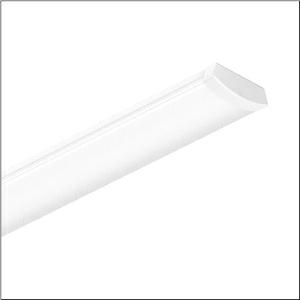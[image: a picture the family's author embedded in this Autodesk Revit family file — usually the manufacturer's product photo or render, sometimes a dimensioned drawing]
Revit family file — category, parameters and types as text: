
# Revit family: siluette_21_51ln12mkm40a
name_source: partatom
category: Lighting Fixtures
units: mm (PartAtom-declared; Revit-internal decimal feet)

## family parameters
Cut with Voids When Loaded = No
Host = Face
Light Source = No
Part Type = Normal
Room Calculation Point = No
Round Connector Dimension = Use Diameter
Shared = No

## types (1)
- --- (1 x LED, 2980 lm, 20.6 W, 5000K)
    Apparent Load = 21 VA
    CIE Flux Codes = 43 73 92 94 100
    Color Rendering = 80
    Color Temperature = 5000K
    Default Elevation = 1800 mm
    Description = Siluette 21, office luminaire, primary optical cover: enclosure, of PC, frosted, light emission: direct distribution, primary light characteristic: symmetric, installation type: suspended mounting, surface-mounted, LED, rated luminous flux: 5.010lm, luminous efficacy: 144lm/W, light colour: 830/840/850, colour temperature: 3000/4000/5000K, control gear: ON/OFF Multilumen, with terminal, 3-pole, mains connection: 220..240V, AC, 50/60Hz, rated input power: 35W, housing, of sheet steel, white, length: 1.200mm, width: 152mm, height: 53mm, end cap, of PMMA, white, protection rating (complete): IP44, insulation class (complete): insulation class I (protective earthing), certification: CE, UKCA, protection symbol: D, impact resistance: IK04, permissible operating ambient temperature: -20..+40°C, contact your sales advisor before using the luminaires in applications with unclear chemical exposure, large temperature fluctuations or condensation-forming humidity, corresponds to IFS (International Featured Standards) requirements for safety and quality in the food industry, packaging unit: 1 piece
    Height = 52 mm  [stored 0.170604 ft]
    Lamp = 1 x LED
    Lamp Light Flux = 2980 lm
    Lamp Power = 20.6 W
    Lamp count = 1
    Length = 1185 mm
    Luminous efficacy = 145 lm/W
    Manufacturer = Siteco
    ModVariant = No
    Model = 51LN12MKM40A
    Mounting Place = Ceiling
    Mounting Type = Pendant
    Number of Poles = 1
    OnlyDefault = Yes
    Power Factor = 1
    Product Name = Siluette 21
    Product group = office luminaire | ceiling pendant
    ProductGroupID = 903
    Protection Class = Protection class I
    Protection Degree = IP 44
    RLX_Detail_Level = 1
    RLX_Emergency_Light_Flux = 0 lm
    RLX_Emergency_Type = 0
    RLX_Emergency_Type_DB = No
    RlxData = <blob elided: 19233 chars, md5=c235beb4>
    Socket = socket
    Standby Power = 0 W
    System Light Flux = 2980 lm
    System Power = 21 W
    Type Comments = individual setting: colour temperature 5000K, luminous flux: 60 % | (OFF | OFF | ON) | 200 mA
    Type Image = l_1296910.jpg
    URL = http://relux.com
    VarID = @adj_067409
    Voltage = 0 V
    Weight = 0.00 kg
    Width = 152 mm

note: [stored X ft] marks values corroborated as IEEE doubles in the binary element streams (Revit-internal decimal feet)

## geometry (parser evidence)
native form markers: Blend x4, Sweep x13
no freeform markers — native parametric forms only
